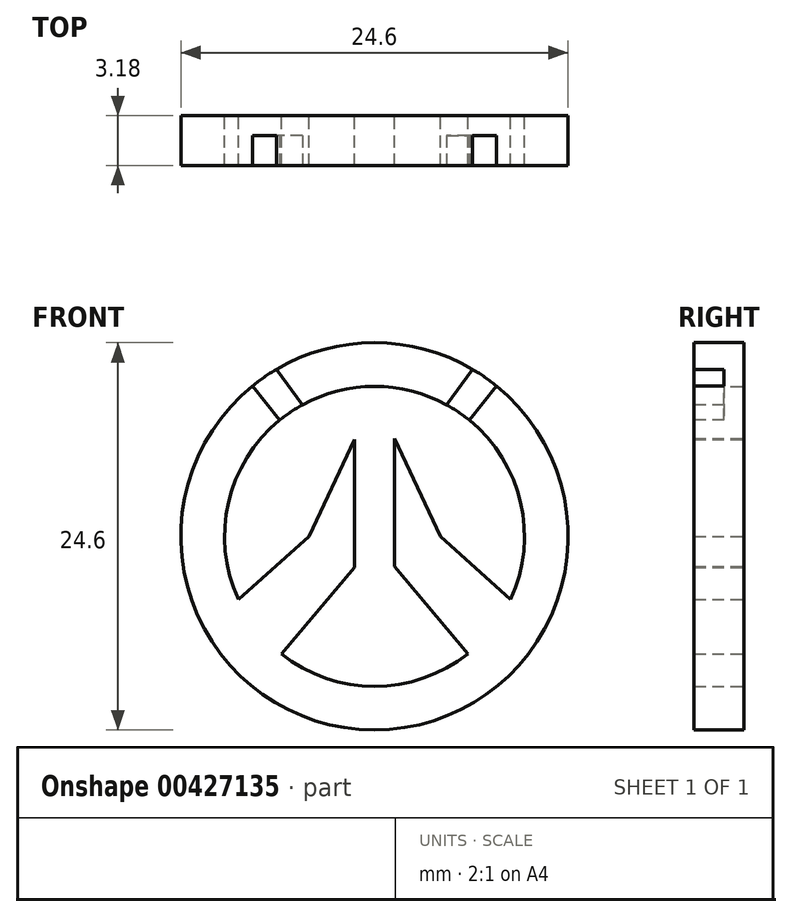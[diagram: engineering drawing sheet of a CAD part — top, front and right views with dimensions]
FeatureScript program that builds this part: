
annotation { "Feature Type Name" : "Feature", "Feature Type Description" : "" }
export const myFeature = defineFeature(function(context is Context, id is Id, definition is map)
    precondition{}
    {
        {
            var Q0;
            Q0=qCreatedBy(makeId("Front.planeOp"),FACE);
            var sketch = newSketch(context, id + "F0", { "sketchPlane" : qUnion([Q0])});
            skCircle(sketch, "E0", {"center": v(0, 0) * mm, "radius": 9.53 * mm});
            skCircle(sketch, "E1", {"center": v(0, 0) * mm, "radius": 12.3 * mm});
            skPoint(sketch, "E2", {"position": v(-1.27, 2.58) * mm});
            skPoint(sketch, "E3", {"position": v(1.27, 2.66) * mm});
            skLineSegment(sketch, "E4", {"start": v(-1.27, -1.98) * mm, "end": v(-5.92, -7.46) * mm});
            skLineSegment(sketch, "E5", {"start": v(1.27, -1.9) * mm, "end": v(5.92, -7.46) * mm});
            skLineSegment(sketch, "E6", {"start": v(-1.27, 2.58) * mm, "end": v(-1.27, 6.15) * mm});
            skLineSegment(sketch, "E7", {"start": v(1.27, 2.66) * mm, "end": v(1.27, 6.22) * mm});
            skLineSegment(sketch, "E8", {"start": v(-1.27, 2.58) * mm, "end": v(-1.27, -1.98) * mm});
            skLineSegment(sketch, "E9", {"start": v(1.27, 2.66) * mm, "end": v(1.27, -1.9) * mm});
            skLineSegment(sketch, "E10", {"start": v(1.27, 6.22) * mm, "end": v(4.2, 0) * mm});
            skLineSegment(sketch, "E11", {"start": v(4.2, 0) * mm, "end": v(8.65, -4) * mm});
            skLineSegment(sketch, "E12", {"start": v(-1.27, 6.15) * mm, "end": v(-4.16, 0) * mm});
            skLineSegment(sketch, "E13", {"start": v(-8.65, -4) * mm, "end": v(-4.16, 0) * mm});
            skSolve(sketch);
        }
        {
            var Q0;
            Q0=makeQuery(id+"F0.imprint","IMPRINT",FACE,{"disambiguationData":[TD([[makeQuery(id+"F0.imprint","IMPRINT",EDGE,{"derivedFrom":sQuery(id+"F0.wireOp",EDGE,"E1")}),1.0]])]});
            var Q1;
            {var subQ0=sQuery(id+"F0.wireOp",EDGE,"E5");Q1=makeQuery(id+"F0.imprint","IMPRINT",FACE,{"disambiguationData":[TD([[makeQuery(id+"F0.imprint","IMPRINT",EDGE,{"derivedFrom":subQ0}),1.0]])]});}
            var Q2;
            {var subQ0=sQuery(id+"F0.wireOp",EDGE,"E4");Q2=makeQuery(id+"F0.imprint","IMPRINT",FACE,{"disambiguationData":[TD([[makeQuery(id+"F0.imprint","IMPRINT",EDGE,{"derivedFrom":subQ0}),-1.0]])]});}
            extrude(context, id + "F1", {"entities" : qUnion([Q0, Q1, Q2]), "depth" : 3.17 * mm});
        }
        {
            var Q0;
            Q0=makeQuery(id+"F1.opExtrude","CAP_FACE",FACE,{"disambiguationData":[OSD([sQuery(id+"F0.wireOp",EDGE,"E0"),sQuery(id+"F0.wireOp",EDGE,"E1"),sQuery(id+"F0.wireOp",EDGE,"E4"),sQuery(id+"F0.wireOp",EDGE,"E5"),sQuery(id+"F0.wireOp",EDGE,"E6"),sQuery(id+"F0.wireOp",EDGE,"E7"),sQuery(id+"F0.wireOp",EDGE,"E8"),sQuery(id+"F0.wireOp",EDGE,"E9"),sQuery(id+"F0.wireOp",EDGE,"E10"),sQuery(id+"F0.wireOp",EDGE,"E11"),sQuery(id+"F0.wireOp",EDGE,"E12"),sQuery(id+"F0.wireOp",EDGE,"E13")])],"isStart":false});
            var sketch = newSketch(context, id + "F2", { "sketchPlane" : qUnion([Q0])});
            skLineSegment(sketch, "E14", {"start": v(-4.58, 8.35) * mm, "end": v(-6.24, 10.6) * mm});
            skLineSegment(sketch, "E15", {"start": v(-6.02, 7.38) * mm, "end": v(-7.75, 9.55) * mm});
            skLineSegment(sketch, "E16", {"start": v(7.75, 9.55) * mm, "end": v(6.02, 7.38) * mm});
            skLineSegment(sketch, "E17", {"start": v(4.58, 8.35) * mm, "end": v(6.24, 10.6) * mm});
            skSolve(sketch);
        }
        {
            var Q0;
            Q0 = qSketchRegion(id + "F2", true);
            var Q1;
            {var subQ0=sQuery(id+"F2.wireOp",EDGE,"E14");Q1=makeQuery(id+"F2.imprint","IMPRINT",FACE,{"disambiguationData":[TD([[makeQuery(id+"F2.imprint","IMPRINT",EDGE,{"derivedFrom":subQ0}),1.0]])]});}
            var Q2;
            {var subQ0=sQuery(id+"F2.wireOp",EDGE,"E16");Q2=makeQuery(id+"F2.imprint","IMPRINT",FACE,{"disambiguationData":[TD([[makeQuery(id+"F2.imprint","IMPRINT",EDGE,{"derivedFrom":subQ0}),-1.0]])]});}
            extrude(context, id + "F3", {"entities" : qUnion([Q0, Q1, Q2]), "operationType" : NewBodyOperationType.REMOVE, "oppositeDirection" : true, "depth" : 1.9 * mm});
        }
    });
